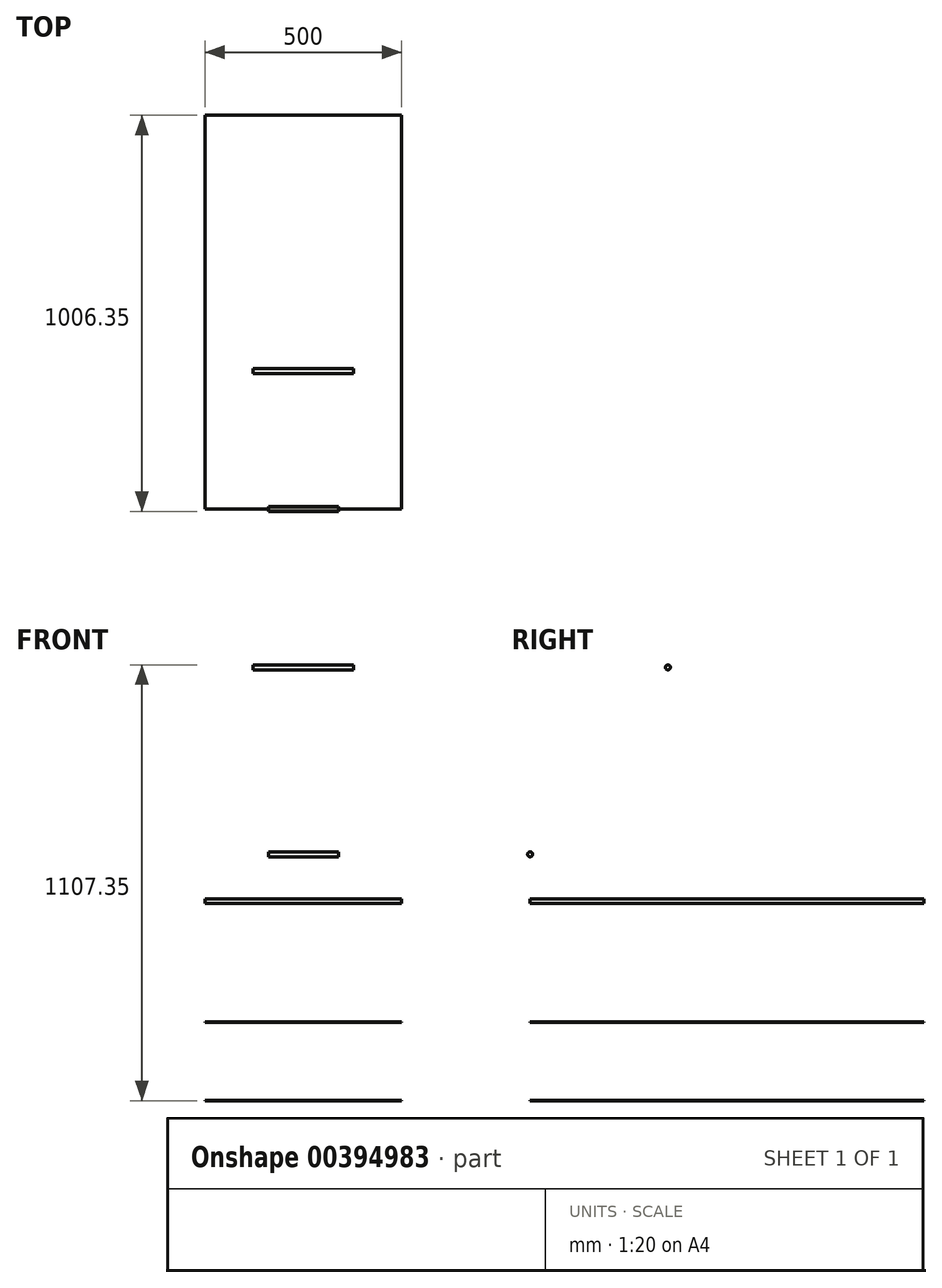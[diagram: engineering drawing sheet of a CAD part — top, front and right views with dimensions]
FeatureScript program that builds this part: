
annotation { "Feature Type Name" : "Feature", "Feature Type Description" : "" }
export const myFeature = defineFeature(function(context is Context, id is Id, definition is map)
    precondition{}
    {
        {
            var Q0;
            Q0=qCreatedBy(makeId("Right.planeOp"),FACE);
            var sketch = newSketch(context, id + "F0", { "sketchPlane" : qUnion([Q0])});
            skCircle(sketch, "E0", {"center": v(0, 0) * mm, "radius": 6.35 * mm});
            skSolve(sketch);
        }
        {
            var Q0;
            Q0=qSketchRegion(id+"F0",true);
            extrude(context, id + "F1", {"entities" : qUnion([Q0]), "endBound" : BoundingType.SYMMETRIC, "depth" : 177.8 * mm});
        }
        {
            var Q0;
            Q0=qCreatedBy(makeId("Right.planeOp"),FACE);
            var sketch = newSketch(context, id + "F2", { "sketchPlane" : qUnion([Q0])});
            skPoint(sketch, "E1.0", {"position": v(0, 0) * mm});
            skLineSegment(sketch, "E2.bottom", {"start": v(0, -114) * mm, "end": v(1000, -114) * mm});
            skLineSegment(sketch, "E2.top", {"start": v(0, -125) * mm, "end": v(1000, -125) * mm});
            skLineSegment(sketch, "E2.left", {"start": v(0, -114) * mm, "end": v(0, -125) * mm});
            skLineSegment(sketch, "E2.right", {"start": v(1000, -114) * mm, "end": v(1000, -125) * mm});
            skLineSegment(sketch, "E3.bottom", {"start": v(0, -427) * mm, "end": v(1000, -427) * mm});
            skLineSegment(sketch, "E3.top", {"start": v(0, -426) * mm, "end": v(1000, -426) * mm});
            skLineSegment(sketch, "E3.left", {"start": v(0, -427) * mm, "end": v(0, -426) * mm});
            skLineSegment(sketch, "E3.right", {"start": v(1000, -427) * mm, "end": v(1000, -426) * mm});
            skLineSegment(sketch, "E4.bottom", {"start": v(0, -626) * mm, "end": v(1000, -626) * mm});
            skLineSegment(sketch, "E4.top", {"start": v(0, -625) * mm, "end": v(1000, -625) * mm});
            skLineSegment(sketch, "E4.left", {"start": v(0, -626) * mm, "end": v(0, -625) * mm});
            skLineSegment(sketch, "E4.right", {"start": v(1000, -626) * mm, "end": v(1000, -625) * mm});
            skSolve(sketch);
        }
        {
            var Q0;
            Q0=qSketchRegion(id+"F2",true);
            extrude(context, id + "F3", {"entities" : qUnion([Q0]), "endBound" : BoundingType.SYMMETRIC, "depth" : 500 * mm});
        }
        {
            var Q0;
            Q0=qCreatedBy(makeId("Right.planeOp"),FACE);
            var sketch = newSketch(context, id + "F4", { "sketchPlane" : qUnion([Q0])});
            skCircle(sketch, "E5", {"center": v(350, 475) * mm, "radius": 6.35 * mm});
            skSolve(sketch);
        }
        {
            var Q0;
            Q0=qSketchRegion(id+"F4",true);
            extrude(context, id + "F5", {"entities" : qUnion([Q0]), "endBound" : BoundingType.SYMMETRIC, "depth" : 254 * mm});
        }
    });
